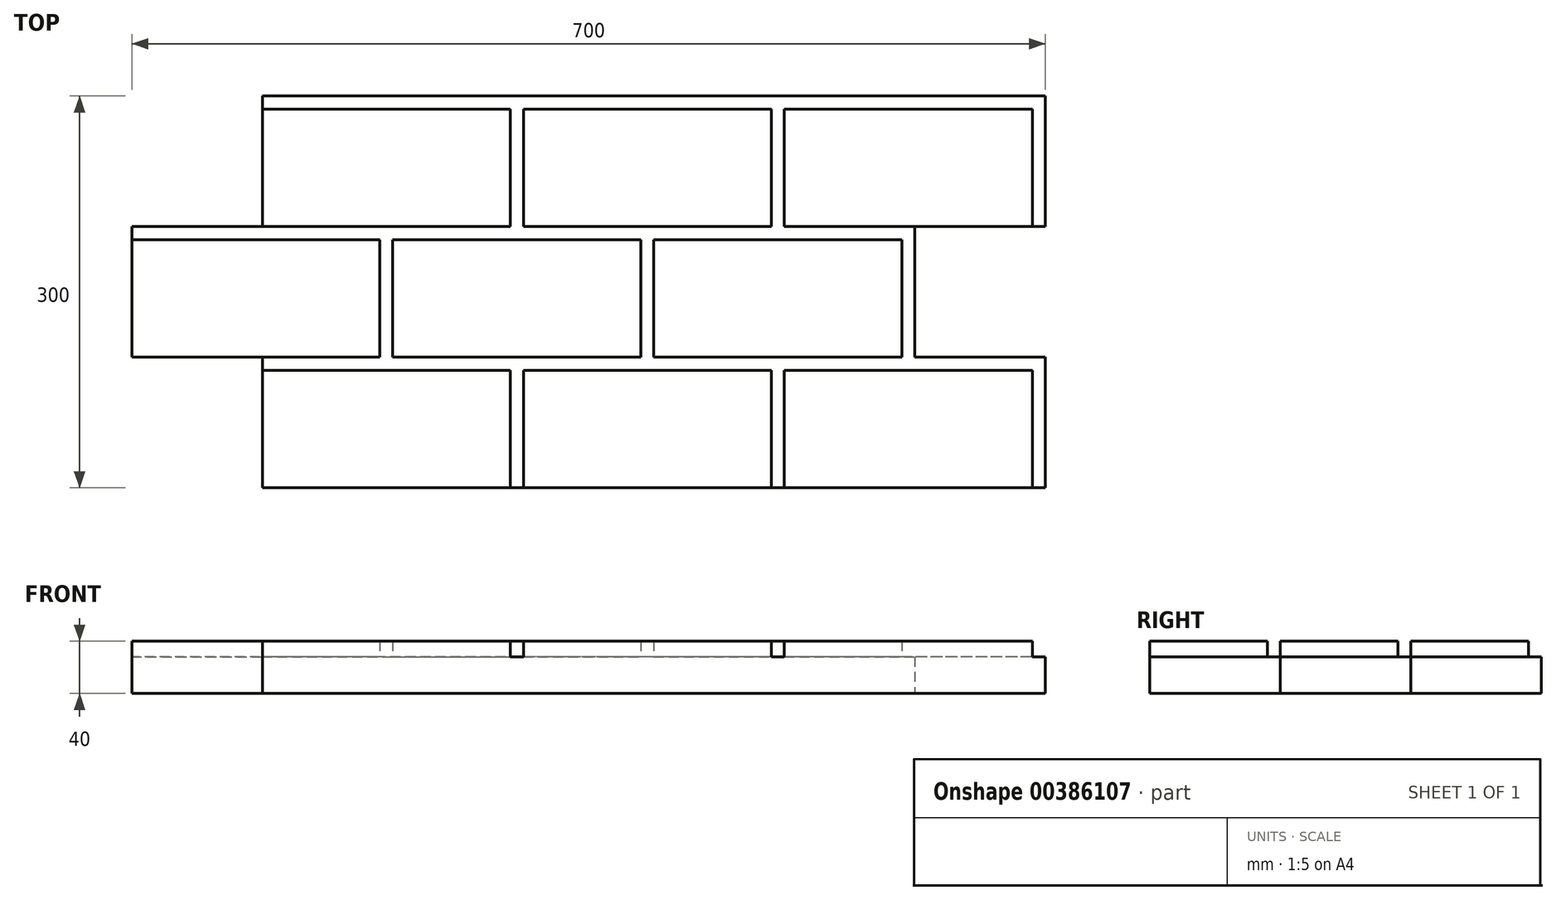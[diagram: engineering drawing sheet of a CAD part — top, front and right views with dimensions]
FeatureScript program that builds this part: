
annotation { "Feature Type Name" : "Feature", "Feature Type Description" : "" }
export const myFeature = defineFeature(function(context is Context, id is Id, definition is map)
    precondition{}
    {
        {
            var Q0;
            Q0=qCreatedBy(makeId("Top.planeOp"),FACE);
            var sketch = newSketch(context, id + "F0", { "sketchPlane" : qUnion([Q0])});
            skLineSegment(sketch, "E0.bottom", {"start": v(350, -150) * mm, "end": v(-250, -150) * mm});
            skLineSegment(sketch, "E0.top", {"start": v(350, 150) * mm, "end": v(-250, 150) * mm});
            skLineSegment(sketch, "E0.left", {"start": v(350, -150) * mm, "end": v(350, -50) * mm});
            skLineSegment(sketch, "E0.right", {"start": v(-350, -50) * mm, "end": v(-350, 50) * mm});
            skPoint(sketch, "E0.middle", {"position": v(0, 0) * mm});
            skLineSegment(sketch, "E1.bottom", {"start": v(350, 50) * mm, "end": v(250, 50) * mm});
            skLineSegment(sketch, "E1.top", {"start": v(350, -50) * mm, "end": v(250, -50) * mm});
            skLineSegment(sketch, "E1.right", {"start": v(250, 50) * mm, "end": v(250, -50) * mm});
            skLineSegment(sketch, "E2.top", {"start": v(-350, 50) * mm, "end": v(-250, 50) * mm});
            skLineSegment(sketch, "E2.right", {"start": v(-250, 150) * mm, "end": v(-250, 50) * mm});
            skLineSegment(sketch, "E3.top", {"start": v(-350, -50) * mm, "end": v(-250, -50) * mm});
            skLineSegment(sketch, "E3.right", {"start": v(-250, -150) * mm, "end": v(-250, -50) * mm});
            skLineSegment(sketch, "E4", {"start": v(0, 0) * mm, "end": v(350, 0) * mm, "construction": true});
            skPoint(sketch, "E5.orphan", {"position": v(-350, 150) * mm});
            skLineSegment(sketch, "E6.trimOffspring", {"start": v(350, 50) * mm, "end": v(350, 150) * mm});
            skPoint(sketch, "E3.left.start.orphan", {"position": v(-350, -150) * mm});
            skSolve(sketch);
        }
        {
            var Q0;
            Q0 = qSketchRegion(id + "F0", true);
            extrude(context, id + "F1", {"entities" : qUnion([Q0]), "depth" : 20 * mm});
        }
        {
            var Q0;
            Q0=makeQuery(id+"F1.opExtrude","CAP_FACE",FACE,{"disambiguationData":[OSD([sQuery(id+"F0.wireOp",EDGE,"E0.bottom"),sQuery(id+"F0.wireOp",EDGE,"E0.top"),sQuery(id+"F0.wireOp",EDGE,"E0.left"),sQuery(id+"F0.wireOp",EDGE,"E0.right"),sQuery(id+"F0.wireOp",EDGE,"E1.bottom"),sQuery(id+"F0.wireOp",EDGE,"E1.top"),sQuery(id+"F0.wireOp",EDGE,"E1.right"),sQuery(id+"F0.wireOp",EDGE,"E2.top"),sQuery(id+"F0.wireOp",EDGE,"E2.right"),sQuery(id+"F0.wireOp",EDGE,"E3.top"),sQuery(id+"F0.wireOp",EDGE,"E3.right"),sQuery(id+"F0.wireOp",EDGE,"E6.trimOffspring")])],"isStart":false});
            var sketch = newSketch(context, id + "F2", { "sketchPlane" : qUnion([Q0])});
            skLineSegment(sketch, "E7.bottom", {"start": v(-350, -50) * mm, "end": v(-160, -50) * mm});
            skLineSegment(sketch, "E7.top", {"start": v(-350, 40) * mm, "end": v(-160, 40) * mm});
            skLineSegment(sketch, "E7.left", {"start": v(-350, -50) * mm, "end": v(-350, 40) * mm});
            skLineSegment(sketch, "E7.right", {"start": v(-160, -50) * mm, "end": v(-160, 40) * mm});
            skLineSegment(sketch, "E8.1.0.0", {"start": v(40, -50) * mm, "end": v(40, 40) * mm});
            skLineSegment(sketch, "E8.1.0.1", {"start": v(-150, -50) * mm, "end": v(-150, 40) * mm});
            skLineSegment(sketch, "E8.1.0.2", {"start": v(-150, 40) * mm, "end": v(40, 40) * mm});
            skLineSegment(sketch, "E8.1.0.3", {"start": v(-150, -50) * mm, "end": v(40, -50) * mm});
            skLineSegment(sketch, "E8.2.0.0", {"start": v(240, -50) * mm, "end": v(240, 40) * mm});
            skLineSegment(sketch, "E8.2.0.1", {"start": v(50, -50) * mm, "end": v(50, 40) * mm});
            skLineSegment(sketch, "E8.2.0.2", {"start": v(50, 40) * mm, "end": v(240, 40) * mm});
            skLineSegment(sketch, "E8.2.0.3", {"start": v(50, -50) * mm, "end": v(240, -50) * mm});
            skLineSegment(sketch, "E8.direction1", {"start": v(-350, -50) * mm, "end": v(-150, -50) * mm, "construction": true});
            skLineSegment(sketch, "E9.bottom", {"start": v(-250, 50) * mm, "end": v(-60, 50) * mm});
            skLineSegment(sketch, "E9.top", {"start": v(-250, 140) * mm, "end": v(-60, 140) * mm});
            skLineSegment(sketch, "E9.left", {"start": v(-250, 50) * mm, "end": v(-250, 140) * mm});
            skLineSegment(sketch, "E9.right", {"start": v(-60, 50) * mm, "end": v(-60, 140) * mm});
            skLineSegment(sketch, "E10.1.0.0", {"start": v(140, 50) * mm, "end": v(140, 140) * mm});
            skLineSegment(sketch, "E10.1.0.1", {"start": v(-50, 50) * mm, "end": v(-50, 140) * mm});
            skLineSegment(sketch, "E10.1.0.2", {"start": v(-50, 140) * mm, "end": v(140, 140) * mm});
            skLineSegment(sketch, "E10.1.0.3", {"start": v(-50, 50) * mm, "end": v(140, 50) * mm});
            skLineSegment(sketch, "E10.2.0.0", {"start": v(340, 50) * mm, "end": v(340, 140) * mm});
            skLineSegment(sketch, "E10.2.0.1", {"start": v(150, 50) * mm, "end": v(150, 140) * mm});
            skLineSegment(sketch, "E10.2.0.2", {"start": v(150, 140) * mm, "end": v(340, 140) * mm});
            skLineSegment(sketch, "E10.2.0.3", {"start": v(150, 50) * mm, "end": v(340, 50) * mm});
            skLineSegment(sketch, "E10.direction1", {"start": v(-250, 50) * mm, "end": v(-50, 50) * mm, "construction": true});
            skLineSegment(sketch, "E11.bottom", {"start": v(-250, -150) * mm, "end": v(-60, -150) * mm});
            skLineSegment(sketch, "E11.top", {"start": v(-250, -60) * mm, "end": v(-60, -60) * mm});
            skLineSegment(sketch, "E11.left", {"start": v(-250, -150) * mm, "end": v(-250, -60) * mm});
            skLineSegment(sketch, "E11.right", {"start": v(-60, -150) * mm, "end": v(-60, -60) * mm});
            skLineSegment(sketch, "E12.1.0.0", {"start": v(140, -150) * mm, "end": v(140, -60) * mm});
            skLineSegment(sketch, "E12.1.0.1", {"start": v(-50, -150) * mm, "end": v(-50, -60) * mm});
            skLineSegment(sketch, "E12.1.0.2", {"start": v(-50, -60) * mm, "end": v(140, -60) * mm});
            skLineSegment(sketch, "E12.1.0.3", {"start": v(-50, -150) * mm, "end": v(140, -150) * mm});
            skLineSegment(sketch, "E12.2.0.0", {"start": v(340, -150) * mm, "end": v(340, -60) * mm});
            skLineSegment(sketch, "E12.2.0.1", {"start": v(150, -150) * mm, "end": v(150, -60) * mm});
            skLineSegment(sketch, "E12.2.0.2", {"start": v(150, -60) * mm, "end": v(340, -60) * mm});
            skLineSegment(sketch, "E12.2.0.3", {"start": v(150, -150) * mm, "end": v(340, -150) * mm});
            skLineSegment(sketch, "E12.direction1", {"start": v(-250, -150) * mm, "end": v(-50, -150) * mm, "construction": true});
            skSolve(sketch);
        }
        {
            var Q0;
            Q0 = qSketchRegion(id + "F2", true);
            extrude(context, id + "F3", {"entities" : qUnion([Q0]), "depth" : 20 * mm});
        }
        {
            var Q0;
            Q0=makeQuery(id+"F1.opExtrude","CAP_FACE",FACE,{"disambiguationData":[OSD([sQuery(id+"F0.wireOp",EDGE,"E0.bottom"),sQuery(id+"F0.wireOp",EDGE,"E0.top"),sQuery(id+"F0.wireOp",EDGE,"E0.left"),sQuery(id+"F0.wireOp",EDGE,"E0.right"),sQuery(id+"F0.wireOp",EDGE,"E1.bottom"),sQuery(id+"F0.wireOp",EDGE,"E1.top"),sQuery(id+"F0.wireOp",EDGE,"E1.right"),sQuery(id+"F0.wireOp",EDGE,"E2.top"),sQuery(id+"F0.wireOp",EDGE,"E2.right"),sQuery(id+"F0.wireOp",EDGE,"E3.top"),sQuery(id+"F0.wireOp",EDGE,"E3.right"),sQuery(id+"F0.wireOp",EDGE,"E6.trimOffspring")])],"isStart":false});
            var sketch = newSketch(context, id + "F4", { "sketchPlane" : qUnion([Q0])});
            skLineSegment(sketch, "E13.0.0", {"start": v(350, 150) * mm, "end": v(-250, 150) * mm});
            skLineSegment(sketch, "E13.0.1", {"start": v(-250, 150) * mm, "end": v(-250, 140) * mm});
            skLineSegment(sketch, "E13.0.2", {"start": v(-250, 50) * mm, "end": v(-350, 50) * mm});
            skLineSegment(sketch, "E13.0.3", {"start": v(-350, 50) * mm, "end": v(-350, 40) * mm});
            skLineSegment(sketch, "E13.0.5", {"start": v(-250, -50) * mm, "end": v(-250, -60) * mm});
            skLineSegment(sketch, "E13.0.6", {"start": v(-60, -150) * mm, "end": v(-50, -150) * mm});
            skLineSegment(sketch, "E13.0.7", {"start": v(350, -150) * mm, "end": v(350, -50) * mm});
            skLineSegment(sketch, "E13.0.8", {"start": v(350, -50) * mm, "end": v(250, -50) * mm});
            skLineSegment(sketch, "E13.0.9", {"start": v(250, -50) * mm, "end": v(250, 50) * mm});
            skLineSegment(sketch, "E13.0.10", {"start": v(340, 50) * mm, "end": v(350, 50) * mm});
            skLineSegment(sketch, "E13.0.11", {"start": v(350, 50) * mm, "end": v(350, 150) * mm});
            skLineSegment(sketch, "E14.0.0", {"start": v(150, 140) * mm, "end": v(150, 50) * mm});
            skLineSegment(sketch, "E14.0.1", {"start": v(150, 50) * mm, "end": v(250, 50) * mm});
            skLineSegment(sketch, "E14.0.2", {"start": v(340, 50) * mm, "end": v(340, 140) * mm});
            skLineSegment(sketch, "E14.0.3", {"start": v(340, 140) * mm, "end": v(150, 140) * mm});
            skLineSegment(sketch, "E15.0.0", {"start": v(50, 40) * mm, "end": v(50, -50) * mm});
            skLineSegment(sketch, "E15.0.1", {"start": v(50, -50) * mm, "end": v(240, -50) * mm});
            skLineSegment(sketch, "E15.0.2", {"start": v(240, -50) * mm, "end": v(240, 40) * mm});
            skLineSegment(sketch, "E15.0.3", {"start": v(240, 40) * mm, "end": v(50, 40) * mm});
            skLineSegment(sketch, "E16.0.0", {"start": v(-150, 40) * mm, "end": v(-150, -50) * mm});
            skLineSegment(sketch, "E16.0.1", {"start": v(-150, -50) * mm, "end": v(40, -50) * mm});
            skLineSegment(sketch, "E16.0.2", {"start": v(40, -50) * mm, "end": v(40, 40) * mm});
            skLineSegment(sketch, "E16.0.3", {"start": v(40, 40) * mm, "end": v(-150, 40) * mm});
            skLineSegment(sketch, "E17.0.0", {"start": v(-50, 140) * mm, "end": v(-50, 50) * mm});
            skLineSegment(sketch, "E17.0.1", {"start": v(-50, 50) * mm, "end": v(140, 50) * mm});
            skLineSegment(sketch, "E17.0.2", {"start": v(140, 50) * mm, "end": v(140, 140) * mm});
            skLineSegment(sketch, "E17.0.3", {"start": v(140, 140) * mm, "end": v(-50, 140) * mm});
            skLineSegment(sketch, "E18.0.0", {"start": v(-60, 140) * mm, "end": v(-250, 140) * mm});
            skLineSegment(sketch, "E18.0.2", {"start": v(-250, 50) * mm, "end": v(-60, 50) * mm});
            skLineSegment(sketch, "E18.0.3", {"start": v(-60, 50) * mm, "end": v(-60, 140) * mm});
            skLineSegment(sketch, "E19.0.0", {"start": v(-160, 40) * mm, "end": v(-350, 40) * mm});
            skLineSegment(sketch, "E19.0.2", {"start": v(-250, -50) * mm, "end": v(-160, -50) * mm});
            skLineSegment(sketch, "E19.0.3", {"start": v(-160, -50) * mm, "end": v(-160, 40) * mm});
            skLineSegment(sketch, "E20.0.1", {"start": v(-60, -150) * mm, "end": v(-60, -60) * mm});
            skLineSegment(sketch, "E20.0.2", {"start": v(-60, -60) * mm, "end": v(-250, -60) * mm});
            skLineSegment(sketch, "E21.0.0", {"start": v(-50, -60) * mm, "end": v(-50, -150) * mm});
            skLineSegment(sketch, "E21.0.2", {"start": v(140, -150) * mm, "end": v(140, -60) * mm});
            skLineSegment(sketch, "E21.0.3", {"start": v(140, -60) * mm, "end": v(-50, -60) * mm});
            skLineSegment(sketch, "E22.0.0", {"start": v(150, -60) * mm, "end": v(150, -150) * mm});
            skLineSegment(sketch, "E22.0.2", {"start": v(340, -150) * mm, "end": v(340, -60) * mm});
            skLineSegment(sketch, "E22.0.3", {"start": v(340, -60) * mm, "end": v(150, -60) * mm});
            skLineSegment(sketch, "E23.trimOffspring", {"start": v(340, -150) * mm, "end": v(350, -150) * mm});
            skLineSegment(sketch, "E24.trimOffspring", {"start": v(140, -150) * mm, "end": v(150, -150) * mm});
            skPoint(sketch, "E20.0.3.end.orphan", {"position": v(-250, -150) * mm});
            skPoint(sketch, "E19.0.1.end.orphan", {"position": v(-350, -50) * mm});
            skSolve(sketch);
        }
        {
            var Q0;
            Q0 = qSketchRegion(id + "F4", true);
            extrude(context, id + "F5", {"entities" : qUnion([Q0]), "operationType" : NewBodyOperationType.ADD, "depth" : 8 * mm});
        }
    });
